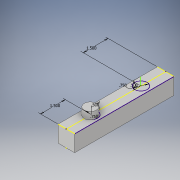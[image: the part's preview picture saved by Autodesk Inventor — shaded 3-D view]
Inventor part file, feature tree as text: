
AUTODESK INVENTOR PART (.ipt)
format: ipt  version: 2017 (Build 210142000, 142)  size: 115,712 bytes
history: native  units: in
note: dims shown in document units (in); Inventor stores cm internally (conversion verified against a paired STEP export)
features: sketch x4, extrude x1, plane x1, revolve x1
ambient origin geometry x8: Origin, YZ Plane, XZ Plane, XY Plane, X Axis, Y Axis, Z Axis, Center Point
bodies: Solid1 (feature_tree)
feature tree (7):
  extrude  "Extrusion1"  Depth=6.0in
  sketch  "Sketch2"  dims[d3=1.0in d4=0.0in d5=0.75in]
  plane  "Work Plane2"
  sketch  "Sketch3"  dims[d6=0.75in]
  revolve  "Revolution1"  [1 undecoded]
  sketch  "Sketch1"  dims[d0=1.0in d2=6.0in]
  sketch  "Sketch4"  dims[d7=1.5in d8=1.5in d11=0.5in d12=0.5in d15=360.0deg]
note: 1 required parameter value undecoded (feature->parameter linkage not recoverable at this tier; creation-order binding heuristic only, values carry confidence <= 0.55)
